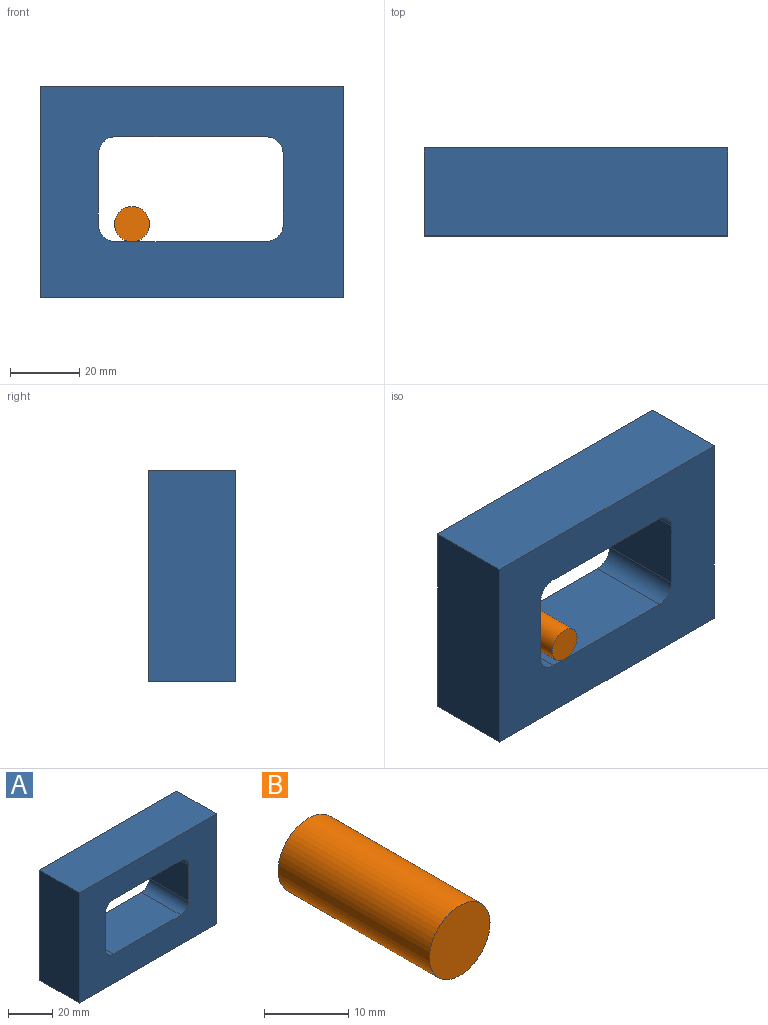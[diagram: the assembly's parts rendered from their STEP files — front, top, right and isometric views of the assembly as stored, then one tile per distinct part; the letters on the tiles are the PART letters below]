
ASSEMBLY  parts=2 mates=1
PART A: 14 faces, bbox 87.9x25.4x61.1 mm
  f0: plane 25.4x20.21mm, normal (1,0,0), area 513.4mm2, adj f8,f9,f10,f13
  f1: plane 43.43x25.4mm, normal (0,0,-1), area 1103mm2, adj f8,f9,f12,f13
  f2: plane 25.4x20.21mm, normal (-1,0,0), area 513.4mm2, adj f8,f9,f11,f12
  f3: plane 61.12x25.4mm, normal (-1,0,0), area 1552.4mm2, adj f4,f6,f8,f9
  f4: plane 87.91x25.4mm, normal (0,0,-1), area 2233mm2, adj f3,f5,f8,f9
  f5: plane 61.12x25.4mm, normal (1,0,0), area 1552.4mm2, adj f4,f6,f8,f9
  f6: plane 87.91x25.4mm, normal (0,0,1), area 2233mm2, adj f3,f5,f8,f9
  f7: plane 43.43x25.4mm, normal (0,0,1), area 1103mm2, adj f8,f9,f10,f11
  f8: plane 87.91x61.12mm, normal (0,-1,0), area 3767.6mm2, adj f0,f1,f2,f3,f4,f5,f6,f7
  f9: plane 87.91x61.12mm, normal (0,1,0), area 3767.6mm2, adj f0,f1,f2,f3,f4,f5,f6,f7
  f10: cylinder r=5.08mm len=25.4mm, axis (0,-1,0), area 202.7mm2, adj f0,f7,f8,f9
  f11: cylinder r=5.08mm len=25.4mm, axis (0,1,0), area 202.7mm2, adj f2,f7,f8,f9
  f12: cylinder r=5.08mm len=25.4mm, axis (0,-1,0), area 202.7mm2, adj f1,f2,f8,f9
  f13: cylinder r=5.08mm len=25.4mm, axis (0,1,0), area 202.7mm2, adj f0,f1,f8,f9
PART B: 3 faces, bbox 10.2x25.4x10.2 mm
  f0: cylinder r=5.09mm len=25.4mm, axis (0,1,0), area 812.5mm2, adj f1,f2
  f1: plane 10.18x10.18mm, normal (0,-1,0), area 81.4mm2, adj f0
  f2: plane 10.18x10.18mm, normal (0,1,0), area 81.4mm2, adj f0
PLACE A t=(47.58,97.3,29.76)mm fixed
PLACE B rot(axis=(0,-1,0),179.8deg) t=(101.91,97.3,82.92)mm
MATE planar B.f0 <-> A.f8  axis (0,-1,0) through (74.16,71.9,51.03)mm
